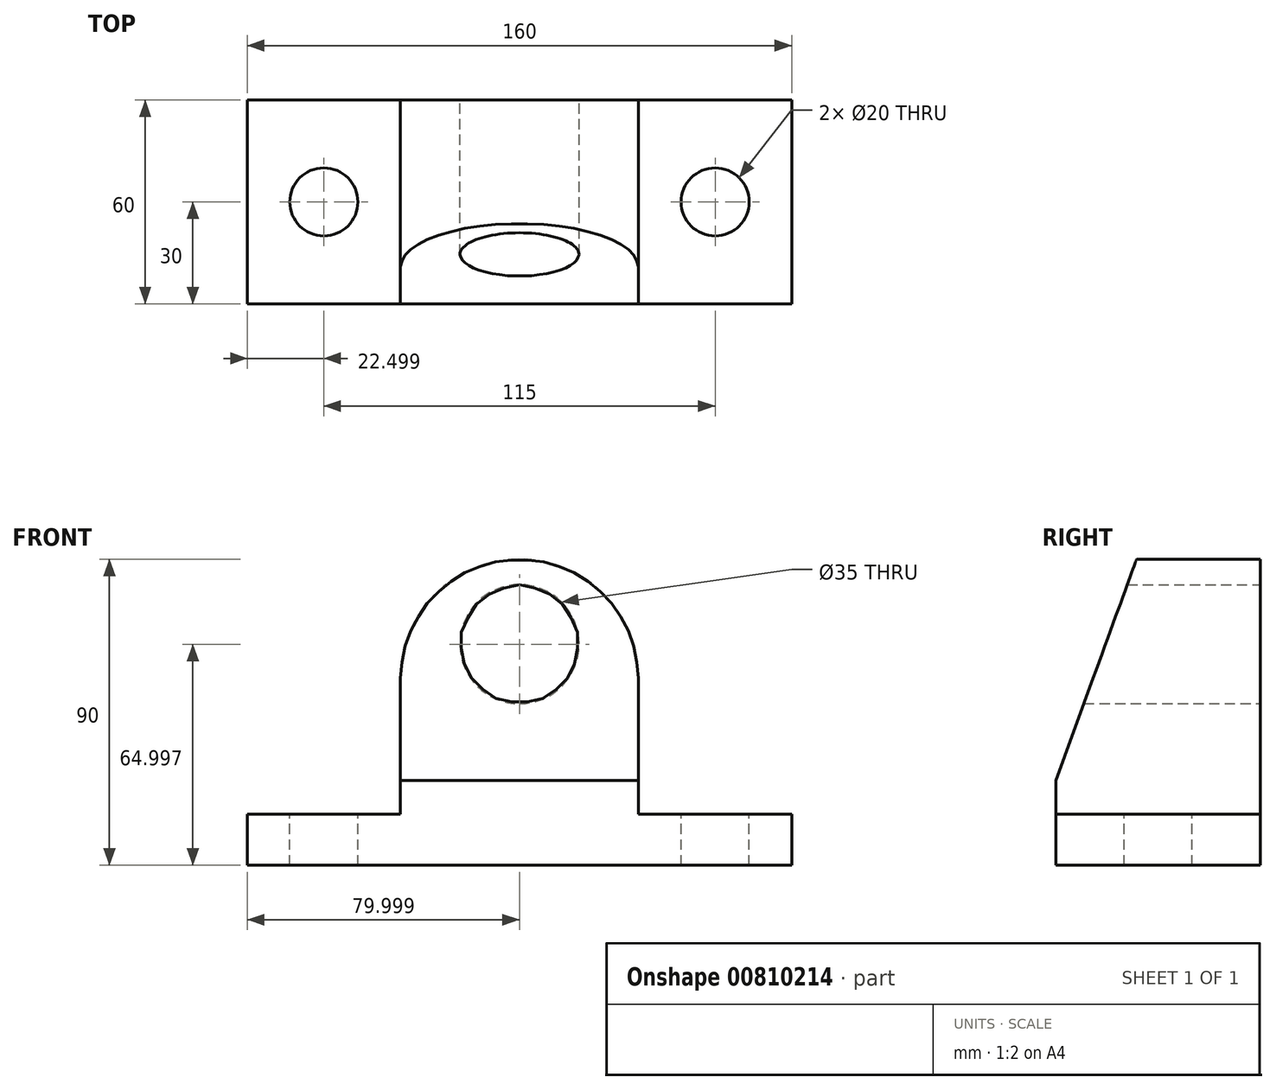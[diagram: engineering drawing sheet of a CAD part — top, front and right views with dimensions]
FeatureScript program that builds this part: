
annotation { "Feature Type Name" : "Feature", "Feature Type Description" : "" }
export const myFeature = defineFeature(function(context is Context, id is Id, definition is map)
    precondition{}
    {
        {
            var Q0;
            Q0=qCreatedBy(makeId("Front.planeOp"),FACE);
            var sketch = newSketch(context, id + "F0", { "sketchPlane" : qUnion([Q0])});
            skLineSegment(sketch, "E0", {"start": v(10.56, -40.8) * mm, "end": v(90.56, -40.8) * mm});
            skLineSegment(sketch, "E1", {"start": v(90.56, -40.8) * mm, "end": v(90.56, -55.8) * mm});
            skLineSegment(sketch, "E2", {"start": v(90.56, -55.8) * mm, "end": v(-69.44, -55.8) * mm});
            skLineSegment(sketch, "E3", {"start": v(-69.44, -55.8) * mm, "end": v(-69.44, -40.8) * mm});
            skLineSegment(sketch, "E4", {"start": v(-69.44, -40.8) * mm, "end": v(13.07, -40.8) * mm});
            skCircle(sketch, "E5", {"center": v(10.56, 9.2) * mm, "radius": 17.5 * mm});
            skLineSegment(sketch, "E6", {"start": v(-69.44, -40.8) * mm, "end": v(-46.94, -40.8) * mm});
            skLineSegment(sketch, "E7", {"start": v(-46.94, -40.8) * mm, "end": v(-46.94, -55.8) * mm});
            skLineSegment(sketch, "E8", {"start": v(90.56, -40.8) * mm, "end": v(68.06, -40.8) * mm});
            skLineSegment(sketch, "E9", {"start": v(68.06, -40.8) * mm, "end": v(68.06, -55.8) * mm});
            skLineSegment(sketch, "E10", {"start": v(-46.94, -40.8) * mm, "end": v(-46.94, -38.01) * mm});
            skLineSegment(sketch, "E11", {"start": v(-24.44, 9.2) * mm, "end": v(-24.44, -40.8) * mm});
            skPoint(sketch, "E11.endSnap0", {"position": v(-28.18, -40.8) * mm});
            skLineSegment(sketch, "E12", {"start": v(45.56, 9.2) * mm, "end": v(45.56, -40.8) * mm});
            skLineSegment(sketch, "E13.bottom", {"start": v(10.56, 9.2) * mm, "end": v(10.56, 9.2) * mm});
            skLineSegment(sketch, "E14.bottom", {"start": v(-24.44, -35.8) * mm, "end": v(45.56, -35.8) * mm});
            skLineSegment(sketch, "E14.top", {"start": v(-24.44, 34.2) * mm, "end": v(45.56, 34.2) * mm});
            skLineSegment(sketch, "E14.left", {"start": v(-24.44, -35.8) * mm, "end": v(-24.44, 34.2) * mm});
            skLineSegment(sketch, "E14.right", {"start": v(45.56, -35.8) * mm, "end": v(45.56, 34.2) * mm});
            skSolve(sketch);
        }
        {
            var Q0;
            Q0 = qSketchRegion(id + "F0", true);
            extrude(context, id + "F1", {"entities" : qUnion([Q0]), "depth" : 60 * mm, "offsetDistance" : 25 * mm});
        }
        {
            var Q0;
            Q0=qCreatedBy(makeId("Top.planeOp"),FACE);
            var sketch = newSketch(context, id + "F2", { "sketchPlane" : qUnion([Q0])});
            skCircle(sketch, "E15", {"center": v(-46.94, -30) * mm, "radius": 10 * mm});
            skCircle(sketch, "E16", {"center": v(68.06, -30) * mm, "radius": 10 * mm});
            skSolve(sketch);
        }
        {
            var Q0;
            Q0=makeQuery(id+"F2.imprint","IMPRINT",FACE,{"disambiguationData":[TD([[makeQuery(id+"F2.imprint","IMPRINT",EDGE,{"derivedFrom":sQuery(id+"F2.wireOp",EDGE,"E15")}),1.0]])]});
            var Q1;
            Q1=makeQuery(id+"F2.imprint","IMPRINT",FACE,{"disambiguationData":[TD([[makeQuery(id+"F2.imprint","IMPRINT",EDGE,{"derivedFrom":sQuery(id+"F2.wireOp",EDGE,"E16")}),1.0]])]});
            extrude(context, id + "F3", {"entities" : qUnion([Q0, Q1]), "operationType" : NewBodyOperationType.REMOVE, "oppositeDirection" : true, "depth" : 75.9 * mm, "offsetDistance" : 25 * mm});
        }
        {
            var Q0;
            Q0=makeQuery(id+"F1.opExtrude","CAP_EDGE",EDGE,{"disambiguationData":[OSD([sQuery(id+"F0.wireOp",EDGE,"E14.top")])],"isStart":false});
            chamfer(context, id + "F4", {"entities" : qUnion([Q0]), "chamferType" : ChamferType.OFFSET_ANGLE, "width" : 65 * mm, "oppositeDirection" : true, "angle" : 20 * degree, "tangentPropagation" : true});
        }
        {
            var Q0;
            Q0=makeQuery(id+"F1.opExtrude","SWEPT_EDGE",EDGE,{"disambiguationData":[OSD([sQuery(id+"F0.wireOp",EDGE,"E14.top"),sQuery(id+"F0.wireOp",EDGE,"E14.right")])]});
            var Q1;
            Q1=makeQuery(id+"F1.opExtrude","SWEPT_EDGE",EDGE,{"disambiguationData":[OSD([sQuery(id+"F0.wireOp",EDGE,"E14.top"),sQuery(id+"F0.wireOp",EDGE,"E14.left")])]});
            fillet(context, id + "F5", {"entities" : qUnion([Q0, Q1]), "radius" : 35 * mm, "tangentPropagation" : true, "allowEdgeOverflow" : false});
        }
    });
